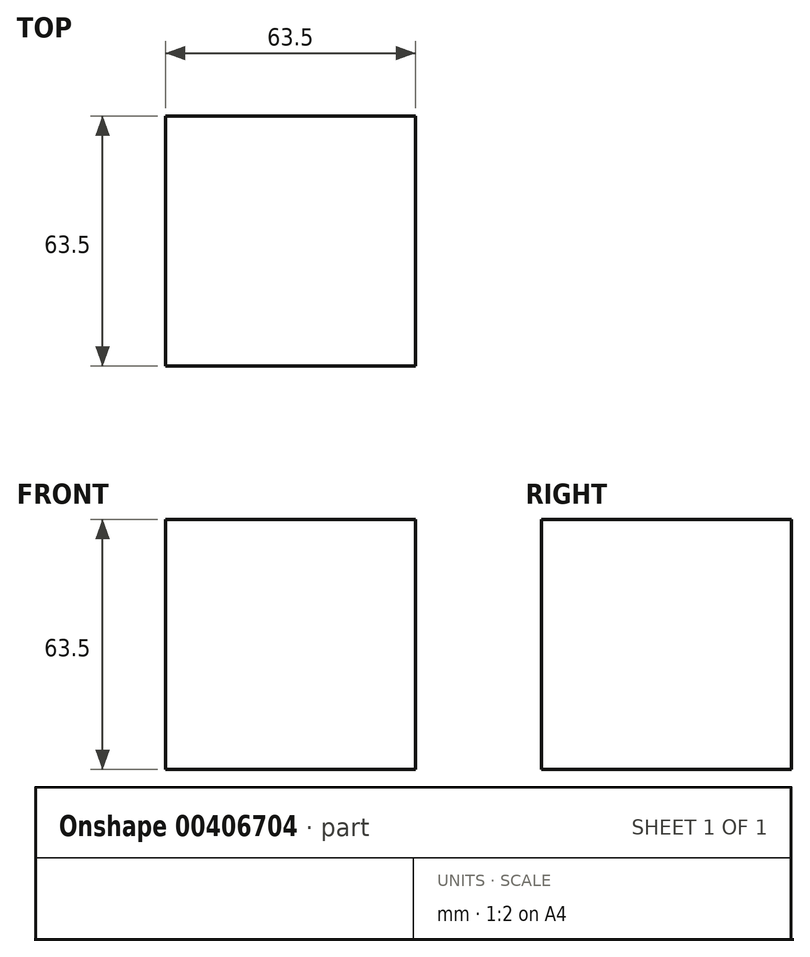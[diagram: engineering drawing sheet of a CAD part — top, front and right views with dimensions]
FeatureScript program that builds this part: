
annotation { "Feature Type Name" : "Feature", "Feature Type Description" : "" }
export const myFeature = defineFeature(function(context is Context, id is Id, definition is map)
    precondition{}
    {
        {
            var Q0;
            Q0=qCreatedBy(makeId("Front.planeOp"),FACE);
            var sketch = newSketch(context, id + "F0", { "sketchPlane" : qUnion([Q0])});
            skLineSegment(sketch, "E0.bottom", {"start": v(0, 0) * mm, "end": v(63.5, 0) * mm});
            skLineSegment(sketch, "E0.top", {"start": v(0, 63.5) * mm, "end": v(63.5, 63.5) * mm});
            skLineSegment(sketch, "E0.left", {"start": v(0, 0) * mm, "end": v(0, 63.5) * mm});
            skLineSegment(sketch, "E0.right", {"start": v(63.5, 0) * mm, "end": v(63.5, 63.5) * mm});
            skSolve(sketch);
        }
        {
            var Q0;
            Q0 = qSketchRegion(id + "F0", true);
            extrude(context, id + "F1", {"entities" : qUnion([Q0]), "depth" : 63.5 * mm});
        }
    });
